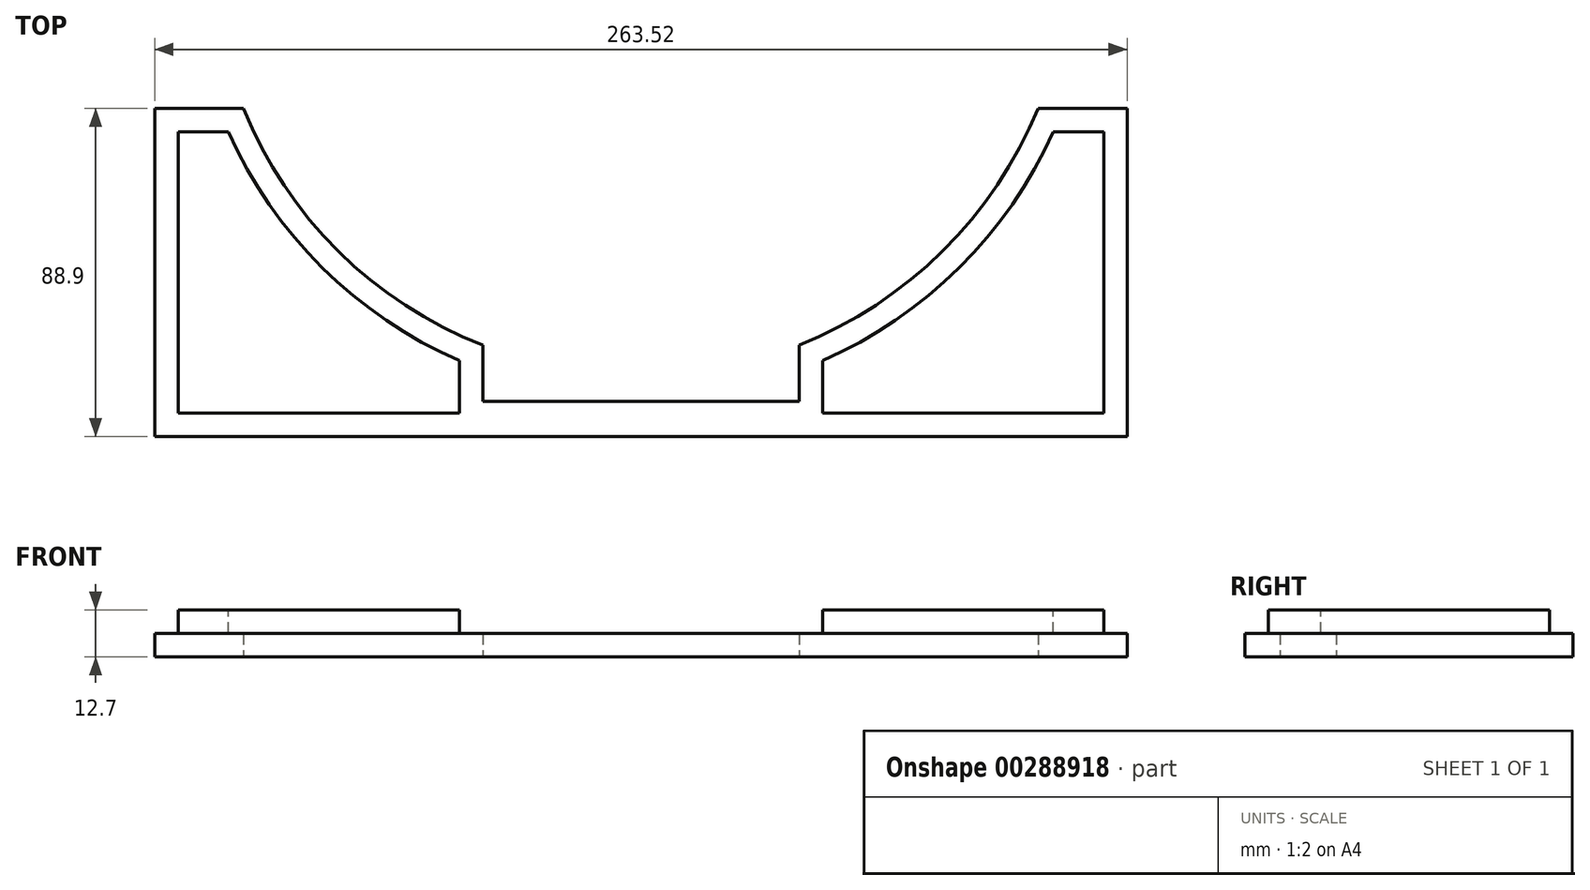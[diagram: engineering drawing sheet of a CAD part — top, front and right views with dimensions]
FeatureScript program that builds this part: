
annotation { "Feature Type Name" : "Feature", "Feature Type Description" : "" }
export const myFeature = defineFeature(function(context is Context, id is Id, definition is map)
    precondition{}
    {
        {
            var Q0;
            Q0=qCreatedBy(makeId("Top.planeOp"),FACE);
            var sketch = newSketch(context, id + "F0", { "sketchPlane" : qUnion([Q0])});
            skLineSegment(sketch, "E0.top", {"start": v(-131.76, -132.83) * mm, "end": v(131.76, -132.83) * mm});
            skLineSegment(sketch, "E0.right", {"start": v(131.76, -43.93) * mm, "end": v(131.76, -132.83) * mm});
            skArc(sketch, "E1", {"start": v(42.86, -108.06) * mm, "mid": v(81.8, -82.6) * mm, "end": v(107.63, -43.93) * mm});
            skLineSegment(sketch, "E2.top", {"start": v(-131.76, -43.93) * mm, "end": v(-107.63, -43.93) * mm});
            skLineSegment(sketch, "E3", {"start": v(-42.86, -123.3) * mm, "end": v(42.86, -123.3) * mm});
            skLineSegment(sketch, "E4.trimOffspring", {"start": v(-42.86, -108.06) * mm, "end": v(-42.86, -123.3) * mm});
            skLineSegment(sketch, "E5.trimOffspring", {"start": v(42.86, -108.06) * mm, "end": v(42.86, -123.3) * mm});
            skLineSegment(sketch, "E6.trimOffspring", {"start": v(107.63, -43.93) * mm, "end": v(131.76, -43.93) * mm});
            skArc(sketch, "E7.trimOffspring", {"start": v(-107.63, -43.93) * mm, "mid": v(-81.92, -82.73) * mm, "end": v(-42.86, -108.06) * mm});
            skLineSegment(sketch, "E8.trimOffspring", {"start": v(-131.76, -43.93) * mm, "end": v(-131.76, -132.83) * mm});
            skPoint(sketch, "E9.top.end.orphan", {"position": v(42.86, -139.82) * mm});
            skPoint(sketch, "E9.top.start.orphan", {"position": v(-42.86, -128.18) * mm});
            skSolve(sketch);
        }
        {
            var Q0;
            Q0 = qSketchRegion(id + "F0", true);
            extrude(context, id + "F1", {"entities" : qUnion([Q0]), "depth" : 12.7 * mm});
        }
        {
            var Q0;
            Q0=makeQuery(id+"F1.opExtrude","CAP_FACE",FACE,{"disambiguationData":[OSD([sQuery(id+"F0.wireOp",EDGE,"E0.top"),sQuery(id+"F0.wireOp",EDGE,"E0.right"),sQuery(id+"F0.wireOp",EDGE,"E1"),sQuery(id+"F0.wireOp",EDGE,"E9.top"),sQuery(id+"F0.wireOp",EDGE,"E2.top"),sQuery(id+"F0.wireOp",EDGE,"E3"),sQuery(id+"F0.wireOp",EDGE,"E4.trimOffspring"),sQuery(id+"F0.wireOp",EDGE,"E5.trimOffspring"),sQuery(id+"F0.wireOp",EDGE,"E6.trimOffspring"),sQuery(id+"F0.wireOp",EDGE,"E7.trimOffspring"),sQuery(id+"F0.wireOp",EDGE,"E8.trimOffspring")])],"isStart":false});
            var sketch = newSketch(context, id + "F2", { "sketchPlane" : qUnion([Q0])});
            skLineSegment(sketch, "E10", {"start": v(-42.86, -108.06) * mm, "end": v(-42.86, -123.3) * mm});
            skLineSegment(sketch, "E11", {"start": v(-42.86, -132.83) * mm, "end": v(-131.76, -132.83) * mm});
            skLineSegment(sketch, "E12", {"start": v(-131.76, -132.83) * mm, "end": v(-131.76, -43.93) * mm});
            skLineSegment(sketch, "E13", {"start": v(-131.76, -43.93) * mm, "end": v(-107.63, -43.93) * mm});
            skArc(sketch, "E14", {"start": v(-107.63, -43.93) * mm, "mid": v(-81.83, -82.64) * mm, "end": v(-42.86, -108.06) * mm});
            skLineSegment(sketch, "E15", {"start": v(42.86, -108.06) * mm, "end": v(42.86, -123.3) * mm});
            skLineSegment(sketch, "E16", {"start": v(42.86, -132.83) * mm, "end": v(131.76, -132.83) * mm});
            skLineSegment(sketch, "E17", {"start": v(131.76, -132.83) * mm, "end": v(131.76, -43.93) * mm});
            skLineSegment(sketch, "E18", {"start": v(131.76, -43.93) * mm, "end": v(107.63, -43.93) * mm});
            skArc(sketch, "E19", {"start": v(42.86, -108.06) * mm, "mid": v(81.8, -82.6) * mm, "end": v(107.63, -43.93) * mm});
            skLineSegment(sketch, "E20.0", {"start": v(-49.21, -112.3) * mm, "end": v(-49.21, -126.48) * mm});
            skArc(sketch, "E20.1", {"start": v(-111.83, -50.28) * mm, "mid": v(-86.31, -87.13) * mm, "end": v(-49.21, -112.3) * mm});
            skLineSegment(sketch, "E20.2", {"start": v(-49.21, -126.48) * mm, "end": v(-125.41, -126.48) * mm});
            skLineSegment(sketch, "E20.3", {"start": v(-125.41, -126.48) * mm, "end": v(-125.41, -50.28) * mm});
            skLineSegment(sketch, "E20.4", {"start": v(-125.41, -50.28) * mm, "end": v(-111.83, -50.28) * mm});
            skArc(sketch, "E21.0", {"start": v(49.21, -112.29) * mm, "mid": v(86.28, -87.1) * mm, "end": v(111.82, -50.28) * mm});
            skLineSegment(sketch, "E21.1", {"start": v(125.41, -50.28) * mm, "end": v(111.82, -50.28) * mm});
            skLineSegment(sketch, "E21.2", {"start": v(49.21, -112.29) * mm, "end": v(49.21, -126.48) * mm});
            skLineSegment(sketch, "E21.3", {"start": v(49.21, -126.48) * mm, "end": v(125.41, -126.48) * mm});
            skLineSegment(sketch, "E21.4", {"start": v(125.41, -126.48) * mm, "end": v(125.41, -50.28) * mm});
            skLineSegment(sketch, "E22", {"start": v(-42.86, -123.3) * mm, "end": v(42.86, -123.3) * mm});
            skSolve(sketch);
        }
        {
            var Q0;
            Q0=makeQuery(id+"F2.imprint","IMPRINT",FACE,{"disambiguationData":[TD([[makeQuery(id+"F2.imprint","IMPRINT",EDGE,{"derivedFrom":sQuery(id+"F2.wireOp",EDGE,"E10")}),-1.0]])]});
            extrude(context, id + "F3", {"entities" : qUnion([Q0]), "operationType" : NewBodyOperationType.REMOVE, "oppositeDirection" : true, "depth" : 6.35 * mm});
        }
    });
